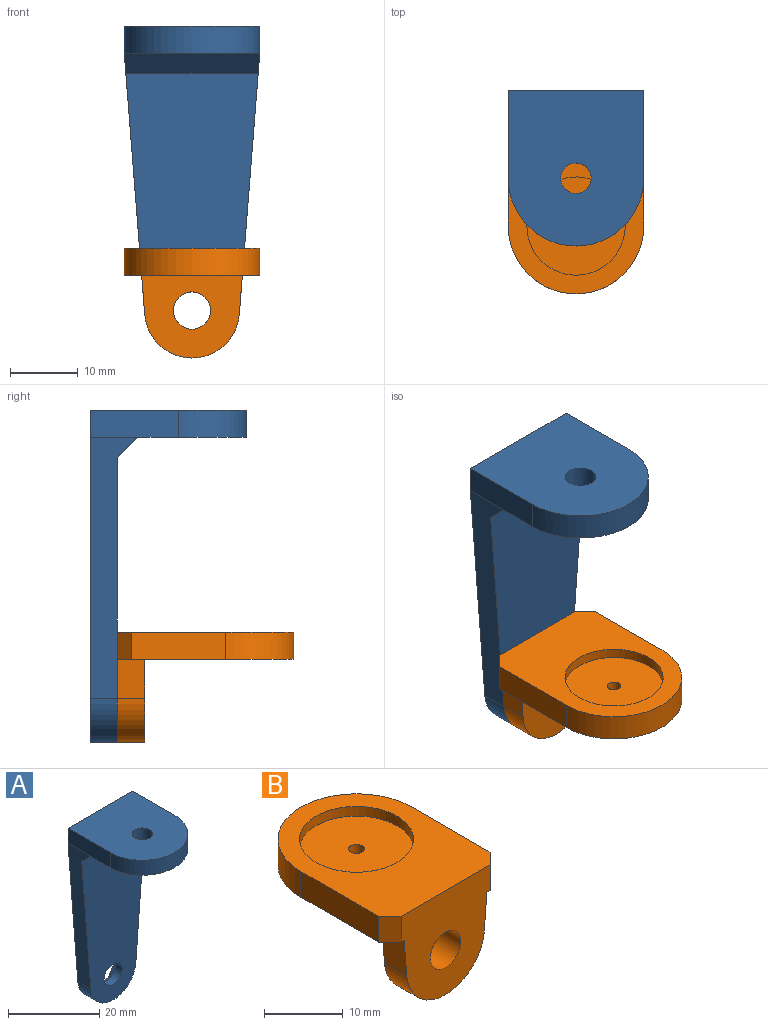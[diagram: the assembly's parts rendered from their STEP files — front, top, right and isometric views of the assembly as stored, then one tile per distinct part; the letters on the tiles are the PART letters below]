
ASSEMBLY  parts=2 mates=1
PART A: 20 faces, bbox 20x23x49 mm
  f0: cylinder r=2.75mm len=5.5mm, axis (0,1,0), area 34.6mm2, adj f1,f19
  f1: plane 42x19.53mm, normal (0,-1,0), area 640.7mm2, adj f0,f3,f4,f5,f12
  f2: plane 13x4mm, normal (-1,0,0), area 52mm2, adj f3,f7,f8,f9,f10
  f3: plane 38.55x7mm, normal (-1,0,-0.08), area 159.2mm2, adj f1,f2,f4,f8,f12
  f4: cylinder r=7mm len=13.96mm, axis (0,1,0), area 83.6mm2, adj f1,f3,f5,f8
  f5: plane 38.55x7mm, normal (1,0,-0.08), area 159.2mm2, adj f1,f4,f6,f8,f12
  f6: plane 13x4mm, normal (1,0,0), area 52mm2, adj f5,f7,f8,f9,f10
  f7: plane 23x20mm, normal (0,0,1), area 401.2mm2, adj f2,f6,f8,f10,f11
  f8: plane 49x20mm, normal (0,1,0), area 741.2mm2, adj f2,f3,f4,f5,f6,f7,f13,f14
  f9: plane 20x16mm, normal (0,0,-1), area 261.2mm2, adj f2,f6,f10,f11,f12
  f10: cylinder r=10mm len=20mm, axis (0,0,1), area 125.7mm2, adj f2,f6,f7,f9
  f11: cylinder r=2.25mm len=4.5mm, axis (0,0,-1), area 56.5mm2, adj f7,f9
  f12: plane 20x3mm, normal (0,-0.71,-0.71), area 83.9mm2, adj f1,f3,f5,f9
  f13: plane 4.25x2.45mm, normal (0.87,0,0.5), area 9.8mm2, adj f8,f14,f18,f19
  f14: plane 4.25x2.45mm, normal (0.87,0,-0.5), area 9.8mm2, adj f8,f13,f15,f19
  f15: plane 4.91x2mm, normal (0,0,-1), area 9.8mm2, adj f8,f14,f16,f19
  f16: plane 4.25x2.45mm, normal (-0.87,0,-0.5), area 9.8mm2, adj f8,f15,f17,f19
  f17: plane 4.25x2.45mm, normal (-0.87,0,0.5), area 9.8mm2, adj f8,f16,f18,f19
  f18: plane 4.91x2mm, normal (0,0,1), area 9.8mm2, adj f8,f13,f17,f19
  f19: plane 9.82x8.5mm, normal (0,1,0), area 38.8mm2, adj f0,f13,f14,f15,f16,f17,f18
PART B: 18 faces, bbox 20x26x16.2 mm
  f0: plane 26x20mm, normal (0,0,-1), area 375.2mm2, adj f1,f3,f4,f6,f8,f9,f10,f15
  f1: plane 5.75x4mm, normal (-1,0,-0.08), area 23.1mm2, adj f0,f2,f8,f9
  f2: cylinder r=7mm len=13.96mm, axis (0,-1,0), area 83.6mm2, adj f1,f3,f8,f9
  f3: plane 5.75x4mm, normal (1,0,-0.08), area 23.1mm2, adj f0,f2,f8,f9
  f4: plane 14x4mm, normal (1,0,0), area 56mm2, adj f0,f5,f10,f17
  f5: plane 26x20mm, normal (0,0,1), area 307.9mm2, adj f4,f6,f9,f10,f11,f16,f17
  f6: plane 14x4mm, normal (-1,0,0), area 56mm2, adj f0,f5,f10,f16
  f7: cylinder r=2.75mm len=5.5mm, axis (0,-1,0), area 69.1mm2, adj f8,f9
  f8: plane 14.86x12.2mm, normal (0,1,0), area 128.4mm2, adj f0,f1,f2,f3,f7
  f9: plane 16.2x16mm, normal (0,-1,0), area 192.4mm2, adj f0,f1,f2,f3,f5,f7,f16,f17
  f10: cylinder r=10mm len=20mm, axis (0,0,1), area 125.7mm2, adj f0,f4,f5,f6
  f11: cylinder r=7.25mm len=14.5mm, axis (0,0,1), area 68.3mm2, adj f5,f12
  f12: plane 14.5x14.5mm, normal (0,0,1), area 162mm2, adj f11,f13
  f13: cylinder r=1mm len=2mm, axis (0,0,1), area 12.6mm2, adj f12,f14
  f14: plane 7x7mm, normal (0,0,-1), area 35.3mm2, adj f13,f15
  f15: cylinder r=3.5mm len=7mm, axis (0,0,-1), area 11mm2, adj f0,f14
  f16: plane 4x2mm, normal (-0.71,-0.71,0), area 11.3mm2, adj f0,f5,f6,f9
  f17: plane 4x2mm, normal (0.71,-0.71,0), area 11.3mm2, adj f0,f4,f5,f9
PLACE A at identity fixed
PLACE B rot(axis=(0,0,1),180deg) t=(0,-4,0)mm
MATE revolute B.f7 <-> A.f4  axis (0,1,0) through (0,-4,0)mm
